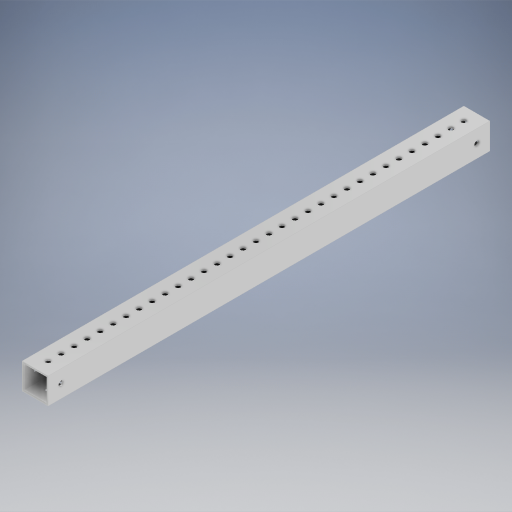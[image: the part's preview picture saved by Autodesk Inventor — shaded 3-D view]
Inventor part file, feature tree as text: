
AUTODESK INVENTOR PART (.ipt)
format: ipt  version: 2024.2 (Build 282272000, 272)  size: 804,864 bytes
history: native  units: in
note: dims shown in document units (in); Inventor stores cm internally (conversion verified against a paired STEP export)
features: other x13, extrude x9, hole x3, pattern_linear x3, mirror x3, sheet_metal_op x1, plane x1
ambient origin geometry x8: Origin, YZ Plane, XZ Plane, XY Plane, X Axis, Y Axis, Z Axis, Center Point
bodies: Solid1 (feature_tree)
feature tree (33):
  other  "Blocks"
  other  "Base Sketch"
  extrude  "Base"  Depth=1.0in
  extrude  "MAX Corner"  Depth=1.0in
  extrude  "MAX Corner Cut"  Depth=0.0625in
  extrude  "Scribe Lines"  Depth=0.0625in
  other  "Side Middle"
  other  "Top Middle"
  other  "Side Holes Sketch"
  hole  "Top Side Hole"  [1 undecoded]
  hole  "Mid Side Hole"  [1 undecoded]
  hole  "Btm Side Hole"  [1 undecoded]
  pattern_linear  "Side Holes"  Spacing1=0.04in  [1 undecoded]
  mirror  "Side Mirror"
  extrude  "MAXTube Hole"  Depth=0.04in
  extrude  "MAXTube Outside"  Depth=17.0in
  pattern_linear  "MAXTube Pattern"  Spacing1=0.0in  [1 undecoded]
  mirror  "MAXTube Mirror"
  extrude  "Left Top Hole"  Depth=17.0in
  extrude  "Mid Top Hole"  TaperAngle=0.0deg  [1 undecoded]
  extrude  "Right Top Hole"  TaperAngle=0.0deg  [1 undecoded]
  pattern_linear  "Top Holes"  Spacing1=0.005in  [1 undecoded]
  mirror  "Top Mirror"
  sheet_metal_op  "Corner"
  other  "MAXTube"
  plane  "Work Plane3"
  other  "Corner:5"
  other  "Corner:6"
  other  "Corner:7"
  other  "Corner:8"
  other  "MAXTube:1"
  other  "MAXTube:2"
  other  "MAXTube:3"
note: 8 required parameter values undecoded (feature->parameter linkage not recoverable at this tier; creation-order binding heuristic only, values carry confidence <= 0.55)
